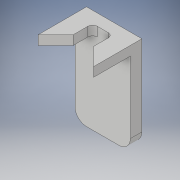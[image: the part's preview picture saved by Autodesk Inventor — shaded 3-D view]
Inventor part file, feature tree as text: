
AUTODESK INVENTOR PART (.ipt)
format: ipt  version: 2017 (Build 210142000, 142)  size: 122,368 bytes
history: native  units: in
note: dims shown in document units (in); Inventor stores cm internally (conversion verified against a paired STEP export)
features: extrude x2, fillet x2, sketch x2, chamfer x1
ambient origin geometry x8: Origin, YZ Plane, XZ Plane, XY Plane, X Axis, Y Axis, Z Axis, Center Point
bodies: Solid1 (feature_tree)
feature tree (7):
  extrude  "Extrusion1"  Depth=1.0in
  extrude  "Extrusion2"  Depth=0.19in
  chamfer  "Chamfer1"  Distance=0.1in
  fillet  "Fillet1"  Radius=0.19in
  fillet  "Fillet2"  Radius=0.4in
  sketch  "Sketch1"  dims[d0=0.6in d1=1.0in]
  sketch  "Sketch2"  dims[d2=0.125in d3=0.0in d4=0.19in d5=0.1in d6=0.19in d7=0.4in d8=0.0in d9=0.19in d10=0.125in d11=45.0deg d12=0.05in d13=0.125in]
